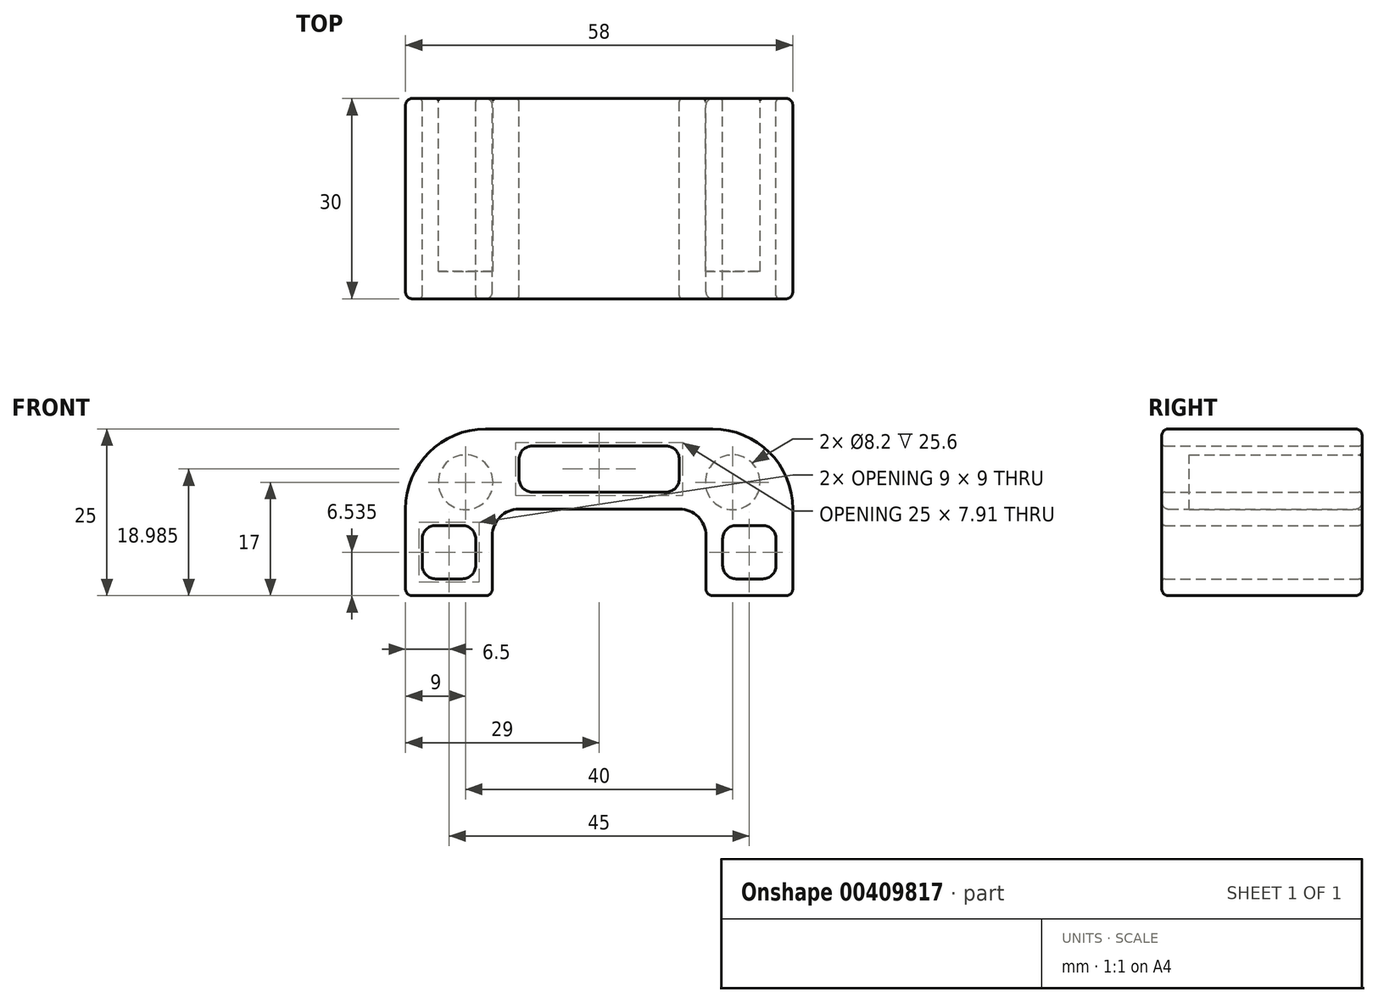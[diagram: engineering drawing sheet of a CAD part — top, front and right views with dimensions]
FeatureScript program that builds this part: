
annotation { "Feature Type Name" : "Feature", "Feature Type Description" : "" }
export const myFeature = defineFeature(function(context is Context, id is Id, definition is map)
    precondition{}
    {
        {
            var Q0;
            Q0=qCreatedBy(makeId("Front.planeOp"),FACE);
            var sketch = newSketch(context, id + "F0", { "sketchPlane" : qUnion([Q0])});
            skCircle(sketch, "E0", {"center": v(-20, 17) * mm, "radius": 4.1 * mm});
            skLineSegment(sketch, "E1", {"start": v(0, 0) * mm, "end": v(0, 26.67) * mm, "construction": true});
            skLineSegment(sketch, "E2", {"start": v(-29, 0) * mm, "end": v(-29, 13) * mm});
            skLineSegment(sketch, "E3", {"start": v(-17, 25) * mm, "end": v(0, 25) * mm});
            skLineSegment(sketch, "E4", {"start": v(-16, 0) * mm, "end": v(-16, 9) * mm});
            skLineSegment(sketch, "E5", {"start": v(-12, 13) * mm, "end": v(0, 13) * mm});
            skPoint(sketch, "E6.visualSharp", {"position": v(-16, 13) * mm});
            skArc(sketch, "E6.filletArc", {"start": v(-12, 13) * mm, "mid": v(-14.83, 11.83) * mm, "end": v(-16, 9) * mm});
            skPoint(sketch, "E7.visualSharp", {"position": v(-29, 25) * mm});
            skArc(sketch, "E7.filletArc", {"start": v(-17, 25) * mm, "mid": v(-25.49, 21.49) * mm, "end": v(-29, 13) * mm});
            skLineSegment(sketch, "E8", {"start": v(-29, 0) * mm, "end": v(-16, 0) * mm});
            skLineSegment(sketch, "E9.MirrorCS", {"start": v(12, 13) * mm, "end": v(0, 13) * mm});
            skArc(sketch, "E10.MirrorCS", {"start": v(12, 13) * mm, "mid": v(14.83, 11.83) * mm, "end": v(16, 9) * mm});
            skLineSegment(sketch, "E11.MirrorCS", {"start": v(16, 0) * mm, "end": v(16, 9) * mm});
            skLineSegment(sketch, "E12.MirrorCS", {"start": v(29, 0) * mm, "end": v(16, 0) * mm});
            skCircle(sketch, "E13.MirrorC", {"center": v(20, 17) * mm, "radius": 4.1 * mm});
            skLineSegment(sketch, "E14.MirrorCS", {"start": v(17, 25) * mm, "end": v(0, 25) * mm});
            skLineSegment(sketch, "E15.MirrorCS", {"start": v(29, 0) * mm, "end": v(29, 13) * mm});
            skArc(sketch, "E16.MirrorCS", {"start": v(17, 25) * mm, "mid": v(25.49, 21.49) * mm, "end": v(29, 13) * mm});
            skLineSegment(sketch, "E17.bottom", {"start": v(10, 22.44) * mm, "end": v(-10, 22.44) * mm});
            skLineSegment(sketch, "E17.top", {"start": v(10, 15.53) * mm, "end": v(-10, 15.53) * mm});
            skLineSegment(sketch, "E17.left", {"start": v(12, 20.44) * mm, "end": v(12, 17.53) * mm});
            skLineSegment(sketch, "E17.right", {"start": v(-12, 20.44) * mm, "end": v(-12, 17.53) * mm});
            skPoint(sketch, "E17.middle", {"position": v(0, 18.98) * mm});
            skPoint(sketch, "E18.visualSharp", {"position": v(-12, 22.44) * mm});
            skArc(sketch, "E18.filletArc", {"start": v(-10, 22.44) * mm, "mid": v(-11.41, 21.85) * mm, "end": v(-12, 20.44) * mm});
            skPoint(sketch, "E19.visualSharp", {"position": v(12, 22.44) * mm});
            skArc(sketch, "E19.filletArc", {"start": v(12, 20.44) * mm, "mid": v(11.41, 21.85) * mm, "end": v(10, 22.44) * mm});
            skPoint(sketch, "E20.visualSharp", {"position": v(12, 15.53) * mm});
            skArc(sketch, "E20.filletArc", {"start": v(10, 15.53) * mm, "mid": v(11.41, 16.12) * mm, "end": v(12, 17.53) * mm});
            skPoint(sketch, "E21.visualSharp", {"position": v(-12, 15.53) * mm});
            skArc(sketch, "E21.filletArc", {"start": v(-12, 17.53) * mm, "mid": v(-11.41, 16.12) * mm, "end": v(-10, 15.53) * mm});
            skLineSegment(sketch, "E22.bottom", {"start": v(20.5, 10.54) * mm, "end": v(24.5, 10.54) * mm});
            skLineSegment(sketch, "E22.top", {"start": v(20.5, 2.54) * mm, "end": v(24.5, 2.54) * mm});
            skLineSegment(sketch, "E22.left", {"start": v(18.5, 8.54) * mm, "end": v(18.5, 4.54) * mm});
            skLineSegment(sketch, "E22.right", {"start": v(26.5, 8.54) * mm, "end": v(26.5, 4.54) * mm});
            skPoint(sketch, "E22.middle", {"position": v(22.5, 6.54) * mm});
            skPoint(sketch, "E22.middle.positionSnap0", {"position": v(22.5, 0) * mm});
            skPoint(sketch, "E22.centerSnap0", {"position": v(22.5, 0) * mm});
            skPoint(sketch, "E23.visualSharp", {"position": v(26.5, 10.54) * mm});
            skArc(sketch, "E23.filletArc", {"start": v(26.5, 8.54) * mm, "mid": v(25.91, 9.95) * mm, "end": v(24.5, 10.54) * mm});
            skPoint(sketch, "E24.visualSharp", {"position": v(18.5, 10.54) * mm});
            skArc(sketch, "E24.filletArc", {"start": v(20.5, 10.54) * mm, "mid": v(19.09, 9.95) * mm, "end": v(18.5, 8.54) * mm});
            skPoint(sketch, "E25.visualSharp", {"position": v(18.5, 2.54) * mm});
            skArc(sketch, "E25.filletArc", {"start": v(18.5, 4.54) * mm, "mid": v(19.09, 3.12) * mm, "end": v(20.5, 2.54) * mm});
            skPoint(sketch, "E26.visualSharp", {"position": v(26.5, 2.54) * mm});
            skArc(sketch, "E26.filletArc", {"start": v(24.5, 2.54) * mm, "mid": v(25.91, 3.12) * mm, "end": v(26.5, 4.54) * mm});
            skArc(sketch, "E27.MirrorCS", {"start": v(-20.5, 10.54) * mm, "mid": v(-19.09, 9.95) * mm, "end": v(-18.5, 8.54) * mm});
            skLineSegment(sketch, "E28.MirrorCS", {"start": v(-20.5, 10.54) * mm, "end": v(-24.5, 10.54) * mm});
            skArc(sketch, "E29.MirrorCS", {"start": v(-26.5, 8.54) * mm, "mid": v(-25.91, 9.95) * mm, "end": v(-24.5, 10.54) * mm});
            skLineSegment(sketch, "E30.MirrorCS", {"start": v(-26.5, 8.54) * mm, "end": v(-26.5, 4.54) * mm});
            skArc(sketch, "E31.MirrorCS", {"start": v(-24.5, 2.54) * mm, "mid": v(-25.91, 3.12) * mm, "end": v(-26.5, 4.54) * mm});
            skLineSegment(sketch, "E32.MirrorCS", {"start": v(-20.5, 2.54) * mm, "end": v(-24.5, 2.54) * mm});
            skArc(sketch, "E33.MirrorCS", {"start": v(-18.5, 4.54) * mm, "mid": v(-19.09, 3.12) * mm, "end": v(-20.5, 2.54) * mm});
            skLineSegment(sketch, "E34.MirrorCS", {"start": v(-18.5, 8.54) * mm, "end": v(-18.5, 4.54) * mm});
            skSolve(sketch);
        }
        {
            var Q0;
            Q0 = qSketchRegion(id + "F0", true);
            extrude(context, id + "F1", {"entities" : qUnion([Q0]), "depth" : 30 * mm});
        }
        {
            var Q0;
            Q0=makeQuery(id+"F1.opExtrude","CAP_FACE",FACE,{"disambiguationData":[OSD([sQuery(id+"F0.wireOp",EDGE,"E0"),sQuery(id+"F0.wireOp",EDGE,"E2"),sQuery(id+"F0.wireOp",EDGE,"E3"),sQuery(id+"F0.wireOp",EDGE,"E4"),sQuery(id+"F0.wireOp",EDGE,"E5"),sQuery(id+"F0.wireOp",EDGE,"E6.filletArc"),sQuery(id+"F0.wireOp",EDGE,"E7.filletArc"),sQuery(id+"F0.wireOp",EDGE,"E8"),sQuery(id+"F0.wireOp",EDGE,"E9.MirrorCS"),sQuery(id+"F0.wireOp",EDGE,"E10.MirrorCS"),sQuery(id+"F0.wireOp",EDGE,"E11.MirrorCS"),sQuery(id+"F0.wireOp",EDGE,"E12.MirrorCS"),sQuery(id+"F0.wireOp",EDGE,"E13.MirrorC"),sQuery(id+"F0.wireOp",EDGE,"E14.MirrorCS"),sQuery(id+"F0.wireOp",EDGE,"E15.MirrorCS"),sQuery(id+"F0.wireOp",EDGE,"E16.MirrorCS")])],"isStart":false});
            var sketch = newSketch(context, id + "F2", { "sketchPlane" : qUnion([Q0])});
            skCircle(sketch, "E35.0", {"center": v(-20, 17) * mm, "radius": 4.1 * mm});
            skCircle(sketch, "E35.1", {"center": v(20, 17) * mm, "radius": 4.1 * mm});
            skSolve(sketch);
        }
        {
            var Q0;
            Q0 = qSketchRegion(id + "F2", true);
            extrude(context, id + "F3", {"entities" : qUnion([Q0]), "operationType" : NewBodyOperationType.ADD, "oppositeDirection" : true, "depth" : 4.1 * mm});
        }
        {
            var Q0;
            Q0=makeQuery(id+"F1.opExtrude","CAP_EDGE",EDGE,{"disambiguationData":[OSD([sQuery(id+"F0.wireOp",EDGE,"E3"),sQuery(id+"F0.wireOp",EDGE,"E14.MirrorCS")])],"isStart":true});
            var Q1;
            Q1=makeQuery(id+"F1.opExtrude","CAP_EDGE",EDGE,{"disambiguationData":[OSD([sQuery(id+"F0.wireOp",EDGE,"E12.MirrorCS")])],"isStart":true});
            var Q2;
            Q2=makeQuery(id+"F1.opExtrude","CAP_EDGE",EDGE,{"disambiguationData":[OSD([sQuery(id+"F0.wireOp",EDGE,"E8")])],"isStart":true});
            var Q3;
            Q3=makeQuery(id+"F1.opExtrude","CAP_EDGE",EDGE,{"disambiguationData":[OSD([sQuery(id+"F0.wireOp",EDGE,"E4")])],"isStart":true});
            var Q4;
            Q4=makeQuery(id+"F1.opExtrude","CAP_EDGE",EDGE,{"disambiguationData":[OSD([sQuery(id+"F0.wireOp",EDGE,"E3"),sQuery(id+"F0.wireOp",EDGE,"E14.MirrorCS")])],"isStart":false});
            var Q5;
            Q5=makeQuery(id+"F1.opExtrude","CAP_EDGE",EDGE,{"disambiguationData":[OSD([sQuery(id+"F0.wireOp",EDGE,"E12.MirrorCS")])],"isStart":false});
            var Q6;
            Q6=makeQuery(id+"F1.opExtrude","CAP_EDGE",EDGE,{"disambiguationData":[OSD([sQuery(id+"F0.wireOp",EDGE,"E8")])],"isStart":false});
            var Q7;
            Q7=makeQuery(id+"F1.opExtrude","CAP_EDGE",EDGE,{"disambiguationData":[OSD([sQuery(id+"F0.wireOp",EDGE,"E4")])],"isStart":false});
            var Q8;
            Q8=makeQuery(id+"F1.opExtrude","SWEPT_EDGE",EDGE,{"disambiguationData":[OSD([sQuery(id+"F0.wireOp",EDGE,"E12.MirrorCS"),sQuery(id+"F0.wireOp",EDGE,"E15.MirrorCS")])]});
            var Q9;
            Q9=makeQuery(id+"F1.opExtrude","SWEPT_EDGE",EDGE,{"disambiguationData":[OSD([sQuery(id+"F0.wireOp",EDGE,"E11.MirrorCS"),sQuery(id+"F0.wireOp",EDGE,"E12.MirrorCS")])]});
            var Q10;
            Q10=makeQuery(id+"F1.opExtrude","SWEPT_EDGE",EDGE,{"disambiguationData":[OSD([sQuery(id+"F0.wireOp",EDGE,"E2"),sQuery(id+"F0.wireOp",EDGE,"E8")])]});
            var Q11;
            Q11=makeQuery(id+"F1.opExtrude","SWEPT_EDGE",EDGE,{"disambiguationData":[OSD([sQuery(id+"F0.wireOp",EDGE,"E4"),sQuery(id+"F0.wireOp",EDGE,"E8")])]});
            fillet(context, id + "F4", {"entities" : qUnion([Q0, Q1, Q2, Q3, Q4, Q5, Q6, Q7, Q8, Q9, Q10, Q11]), "radius" : 1 * mm, "tangentPropagation" : true, "allowEdgeOverflow" : false});
        }
        {
            var Q0;
            Q0=makeQuery(id+"F1.opExtrude","CAP_EDGE",EDGE,{"disambiguationData":[OSD([sQuery(id+"F0.wireOp",EDGE,"E13.MirrorC")])],"isStart":true});
            var Q1;
            Q1=makeQuery(id+"F1.opExtrude","CAP_EDGE",EDGE,{"disambiguationData":[OSD([sQuery(id+"F0.wireOp",EDGE,"E0")])],"isStart":true});
            fillet(context, id + "F5", {"entities" : qUnion([Q0, Q1]), "radius" : .3 * mm, "tangentPropagation" : true, "allowEdgeOverflow" : false});
        }
        {
            var Q0;
            Q0=makeQuery(id+"F1.opExtrude","CAP_EDGE",EDGE,{"disambiguationData":[OSD([sQuery(id+"F0.wireOp",EDGE,"E22.bottom")])],"isStart":false});
            var Q1;
            Q1=makeQuery(id+"F1.opExtrude","CAP_EDGE",EDGE,{"disambiguationData":[OSD([sQuery(id+"F0.wireOp",EDGE,"E28.MirrorCS")])],"isStart":false});
            var Q2;
            Q2=makeQuery(id+"F1.opExtrude","CAP_EDGE",EDGE,{"disambiguationData":[OSD([sQuery(id+"F0.wireOp",EDGE,"E22.bottom")])],"isStart":true});
            var Q3;
            Q3=makeQuery(id+"F1.opExtrude","CAP_EDGE",EDGE,{"disambiguationData":[OSD([sQuery(id+"F0.wireOp",EDGE,"E28.MirrorCS")])],"isStart":true});
            var Q4;
            Q4=makeQuery(id+"F1.opExtrude","CAP_EDGE",EDGE,{"disambiguationData":[OSD([sQuery(id+"F0.wireOp",EDGE,"E17.top")])],"isStart":true});
            var Q5;
            Q5=makeQuery(id+"F1.opExtrude","CAP_EDGE",EDGE,{"disambiguationData":[OSD([sQuery(id+"F0.wireOp",EDGE,"E17.bottom")])],"isStart":false});
            fillet(context, id + "F6", {"entities" : qUnion([Q0, Q1, Q2, Q3, Q4, Q5]), "radius" : .5 * mm, "tangentPropagation" : true, "allowEdgeOverflow" : false});
        }
    });
